# Revit family: PV_Compact_DN050_ 20-80_FF_měř-vyp_RFA_2019
name_source: partatom
category: Pipe Accessories
units: mm (PartAtom-declared; Revit-internal decimal feet)

## family parameters
Always vertical = Yes
Cut with Voids When Loaded = No
Part Type = Valve - Breaks Into
Round Connector Dimension = Use Diameter
Shared = No
Work Plane-Based = No

## types (10) — shared parameters
C0D0 = No
C0D1 = Yes
CAT0 = Yes
DR0 = No
DR1 = Yes
Description = Nastavitelný regulátor tlakové diference
L2D = 65 mm
L2D_Min = 30 mm
MC Pressure Drop Maximum Value = 0.0 Pa
MC Pressure Drop Minimum Value = 0.0 Pa
MC Use Limits From Balancing Method = No
Manufacturer = Hydronic Systems Prague s.r.o.
QmdConnectorList = 301;D;302;D
R3 = 10 mm  [stored 0.0328084 ft]
R4 = 15 mm  [stored 0.0492126 ft]
R5 = 5 mm  [stored 0.0164042 ft]
Type Comments = závitový s vnitřním závitem; s měřicí vsuvkou a vypouštěním; PN25; dpmax=450kPa; -10~+120°C
URL = www.hydronic.cz
W2D = 15 mm  [stored 0.0492126 ft]
Z7 = 15 mm  [stored 0.0492126 ft]
magiPartTypeId = 304
magiProductFamilyId = 88c57951ecb64b5d83dd1d4eb8fc72
zero-valued in all types: MC Throttling Maximum Value, MC Throttling Minimum Value

## per-type parameters (varying)
- PV Compact DN15 FF s měřením a vypouštěním (20-60kPa): CenSd_R2_6=12 mm  [stored 0.0393701 ft]; D=15 mm; DL2=66 mm; L3=11 mm  [stored 0.0360892 ft]; LL=6 mm  [stored 0.019685 ft]; LL2=32 mm; LLT=15 mm  [stored 0.0492126 ft]; LLT__ve=-15 mm  [stored -0.0492126 ft]; LL__ve=-6 mm; LM=45 mm; LP=38 mm; M2=23 mm; M3=25 mm  [stored 0.082021 ft]; M4=31 mm; M5=33 mm; MC Product Code=53-3243 DN15; FF; nastavitelný rozsah dp=20~60kPa; Q=100~1000l/h;  kvs=2,9; NL=15 mm  [stored 0.0492126 ft]; NL__ve=-15 mm  [stored -0.0492126 ft]; PH=22 mm; PH__ve=-22 mm; R1=19 mm  [stored 0.062336 ft]; R2=14 mm  [stored 0.0459318 ft]; XR1=13 mm  [stored 0.0426509 ft]; XR2=25 mm  [stored 0.082021 ft]; XR3=30 mm; Z2=41 mm; Z3=8 mm  [stored 0.0262467 ft]; Z4=49 mm; Z5=57 mm; Z6=25 mm  [stored 0.082021 ft]; magiProductId=ebd4dd38c61a47e78db1b31e427098
- PV Compact DN15 FF s měřením a vypouštěním ( 5-30kPa): CenSd_R2_6=12 mm  [stored 0.0393701 ft]; D=15 mm; DL2=66 mm; L3=11 mm  [stored 0.0360892 ft]; LL=6 mm  [stored 0.019685 ft]; LL2=32 mm; LLT=15 mm  [stored 0.0492126 ft]; LLT__ve=-15 mm  [stored -0.0492126 ft]; LL__ve=-6 mm; LM=45 mm; LP=38 mm; M2=23 mm; M3=25 mm  [stored 0.082021 ft]; M4=31 mm; M5=33 mm; MC Product Code=53-3242 DN15; FF; nastavitelný rozsah dp=5~30kPa; Q=50~600l/h;  kvs=2,9; NL=15 mm  [stored 0.0492126 ft]; NL__ve=-15 mm  [stored -0.0492126 ft]; PH=22 mm; PH__ve=-22 mm; R1=19 mm  [stored 0.062336 ft]; R2=14 mm  [stored 0.0459318 ft]; XR1=13 mm  [stored 0.0426509 ft]; XR2=25 mm  [stored 0.082021 ft]; XR3=30 mm; Z2=41 mm; Z3=8 mm  [stored 0.0262467 ft]; Z4=49 mm; Z5=57 mm; Z6=25 mm  [stored 0.082021 ft]; magiProductId=1e13aaf8f1b54965adca1ab26bd771
- PV Compact DN20 FF s měřením a vypouštěním (20-60kPa): CenSd_R2_6=12 mm  [stored 0.0393701 ft]; D=20 mm; DL2=66 mm; L3=11 mm  [stored 0.0360892 ft]; LL=6 mm  [stored 0.019685 ft]; LL2=32 mm; LLT=15 mm  [stored 0.0492126 ft]; LLT__ve=-15 mm  [stored -0.0492126 ft]; LL__ve=-6 mm; LM=47 mm; LP=40 mm; M2=24 mm; M3=26 mm; M4=32 mm; M5=34 mm; MC Product Code=53-3245 DN20; FF; nastavitelný rozsah dp=20~60kPa; Q=150~2000l/h;  kvs=3,5; NL=16 mm; NL__ve=-16 mm; PH=22 mm; PH__ve=-22 mm; R1=19 mm  [stored 0.062336 ft]; R2=14 mm  [stored 0.0459318 ft]; XR1=13 mm  [stored 0.0426509 ft]; XR2=25 mm  [stored 0.082021 ft]; XR3=30 mm; Z2=41 mm; Z3=8 mm  [stored 0.0262467 ft]; Z4=49 mm; Z5=57 mm; Z6=25 mm  [stored 0.082021 ft]; magiProductId=6d4e29c475624129ae1d8630218e83
- PV Compact DN20 FF s měřením a vypouštěním ( 5-30kPa): CenSd_R2_6=12 mm  [stored 0.0393701 ft]; D=20 mm; DL2=66 mm; L3=11 mm  [stored 0.0360892 ft]; LL=6 mm  [stored 0.019685 ft]; LL2=32 mm; LLT=15 mm  [stored 0.0492126 ft]; LLT__ve=-15 mm  [stored -0.0492126 ft]; LL__ve=-6 mm; LM=47 mm; LP=40 mm; M2=24 mm; M3=26 mm; M4=32 mm; M5=34 mm; MC Product Code=53-3244 DN20; FF; nastavitelný rozsah dp=5~30kPa; Q=100~1000l/h;  kvs=3,5; NL=16 mm; NL__ve=-16 mm; PH=22 mm; PH__ve=-22 mm; R1=19 mm  [stored 0.062336 ft]; R2=14 mm  [stored 0.0459318 ft]; XR1=13 mm  [stored 0.0426509 ft]; XR2=25 mm  [stored 0.082021 ft]; XR3=30 mm; Z2=41 mm; Z3=8 mm  [stored 0.0262467 ft]; Z4=49 mm; Z5=57 mm; Z6=25 mm  [stored 0.082021 ft]; magiProductId=3c7d936801344d2a9486b3d5f20c15
- PV Compact DN25 FF s měřením a vypouštěním ( 5-30kPa): CenSd_R2_6=12 mm  [stored 0.0393701 ft]; D=25 mm; DL2=68 mm; L3=11 mm  [stored 0.0360892 ft]; LL=6 mm  [stored 0.019685 ft]; LL2=34 mm; LLT=16 mm; LLT__ve=-16 mm; LL__ve=-6 mm; LM=50 mm; LP=42 mm; M2=25 mm  [stored 0.082021 ft]; M3=27 mm; M4=33 mm; M5=35 mm; MC Product Code=53-3251 DN25; FF; nastavitelný rozsah dp=5~30kPa; Q=600~2100l/h;  kvs=4,0; NL=17 mm; NL__ve=-17 mm  [stored -0.0557743 ft]; PH=23 mm; PH__ve=-23 mm; R1=19 mm  [stored 0.062336 ft]; R2=14 mm  [stored 0.0459318 ft]; XR1=13 mm  [stored 0.0426509 ft]; XR2=25 mm  [stored 0.082021 ft]; XR3=30 mm; Z2=43 mm; Z3=9 mm  [stored 0.0295276 ft]; Z4=51 mm; Z5=60 mm; Z6=26 mm; magiProductId=40b783a088714ff8af367f7ba18a04
- PV Compact DN25L FF s měřením a vypouštěním (20-80kPa): CenSd_R2_6=23 mm; D=25 mm; DL2=72 mm; L3=11 mm  [stored 0.0360892 ft]; LL=6 mm  [stored 0.019685 ft]; LL2=38 mm; LLT=19 mm  [stored 0.062336 ft]; LLT__ve=-19 mm; LL__ve=-6 mm; LM=60 mm; LP=50 mm; M2=30 mm; M3=32 mm; M4=38 mm; M5=40 mm; MC Product Code=53-3247 DN25; FF; nastavitelný rozsah dp=20~80kPa; Q=750~4200l/h;  kvs=8,7; NL=20 mm  [stored 0.0656168 ft]; NL__ve=-20 mm  [stored -0.0656168 ft]; PH=24 mm; PH__ve=-24 mm; R1=32 mm; R2=27 mm; XR1=26 mm; XR2=38 mm; XR3=43 mm; Z2=67 mm; Z3=13 mm  [stored 0.0426509 ft]; Z4=80 mm; Z5=94 mm; Z6=40 mm; magiProductId=7052257d0cc94620b8f60c4ac85ccd
- PV Compact DN25L FF s měřením a vypouštěním ( 5-30kPa): CenSd_R2_6=23 mm; D=25 mm; DL2=72 mm; L3=11 mm  [stored 0.0360892 ft]; LL=6 mm  [stored 0.019685 ft]; LL2=38 mm; LLT=19 mm  [stored 0.062336 ft]; LLT__ve=-19 mm; LL__ve=-6 mm; LM=60 mm; LP=50 mm; M2=30 mm; M3=32 mm; M4=38 mm; M5=40 mm; MC Product Code=53-3246 DN25L; FF; nastavitelný rozsah dp=5~30kPa; Q=600~2500l/h;  kvs=8,7; NL=20 mm  [stored 0.0656168 ft]; NL__ve=-20 mm  [stored -0.0656168 ft]; PH=24 mm; PH__ve=-24 mm; R1=32 mm; R2=27 mm; XR1=26 mm; XR2=38 mm; XR3=43 mm; Z2=67 mm; Z3=13 mm  [stored 0.0426509 ft]; Z4=80 mm; Z5=94 mm; Z6=40 mm; magiProductId=006ff7ff77e34fd39e52f3f4c37192
- PV Compact DN32 FF s měřením a vypouštěním (20-80kPa): CenSd_R2_6=23 mm; D=32 mm; DL2=77 mm; L3=25 mm  [stored 0.082021 ft]; LL=7 mm  [stored 0.0229659 ft]; LL2=43 mm; LLT=23 mm; LLT__ve=-23 mm; LL__ve=-7 mm  [stored -0.0229659 ft]; LM=62 mm; LP=52 mm; M2=31 mm; M3=33 mm; M4=39 mm; M5=41 mm; MC Product Code=53-3248 DN32; FF; nastavitelný rozsah dp=20~80kPa; Q=1000~5000l/h;  kvs=10,1; NL=21 mm; NL__ve=-21 mm; PH=25 mm  [stored 0.082021 ft]; PH__ve=-25 mm  [stored -0.082021 ft]; R1=32 mm; R2=27 mm; XR1=26 mm; XR2=38 mm; XR3=43 mm; Z2=67 mm; Z3=13 mm  [stored 0.0426509 ft]; Z4=80 mm; Z5=94 mm; Z6=40 mm; magiProductId=e53839f5e58040c69ad69dcf8b7122
- PV Compact DN40 FF s měřením a vypouštěním (20-80kPa): CenSd_R2_6=23 mm; D=40 mm; DL2=80 mm; L3=25 mm  [stored 0.082021 ft]; LL=7 mm  [stored 0.0229659 ft]; LL2=46 mm; LLT=25 mm  [stored 0.082021 ft]; LLT__ve=-25 mm  [stored -0.082021 ft]; LL__ve=-7 mm  [stored -0.0229659 ft]; LM=83 mm; LP=69 mm; M2=41 mm; M3=43 mm; M4=49 mm; M5=51 mm; MC Product Code=53-3249 DN40; FF; nastavitelný rozsah dp=20~80kPa; Q=3000~8000l/h;  kvs=15,8; NL=28 mm  [stored 0.0918635 ft]; NL__ve=-28 mm; PH=25 mm  [stored 0.082021 ft]; PH__ve=-25 mm  [stored -0.082021 ft]; R1=32 mm; R2=27 mm; XR1=26 mm; XR2=38 mm; XR3=43 mm; Z2=78 mm; Z3=16 mm; Z4=94 mm; Z5=109 mm; Z6=47 mm; magiProductId=edae53f0ee9843aa9c005a0dbc2db4
- PV Compact DN50 FF s měřením a vypouštěním (20-80kPa): CenSd_R2_6=31 mm; D=50 mm; DL2=86 mm; L3=25 mm  [stored 0.082021 ft]; LL=8 mm  [stored 0.0262467 ft]; LL2=52 mm; LLT=29 mm; LLT__ve=-29 mm; LL__ve=-8 mm; LM=83 mm; LP=69 mm; M2=41 mm; M3=43 mm; M4=49 mm; M5=51 mm; MC Product Code=53-3250 DN50; FF; nastavitelný rozsah dp=20~80kPa; Q=5000~11500l/h;  kvs=16,2; NL=28 mm  [stored 0.0918635 ft]; NL__ve=-28 mm; PH=26 mm; PH__ve=-26 mm; R1=32 mm; R2=35 mm; XR1=26 mm; XR2=38 mm; XR3=43 mm; Z2=78 mm; Z3=16 mm; Z4=94 mm; Z5=109 mm; Z6=47 mm; magiProductId=7572286e99104aaeaae4a504f9a6dd

note: [stored X ft] marks values corroborated as IEEE doubles in the binary element streams (Revit-internal decimal feet)

## geometry (parser evidence)
native form markers: Sweep x1
no freeform markers — native parametric forms only
